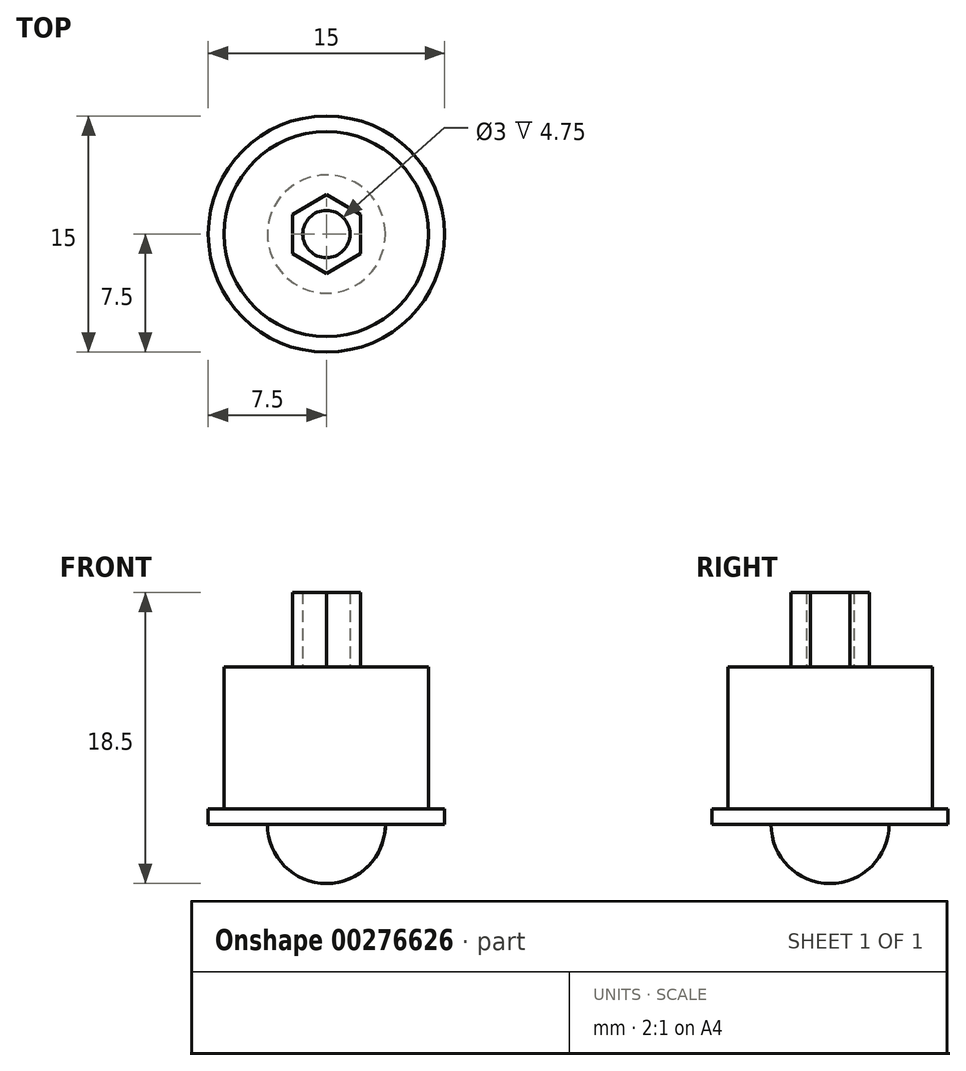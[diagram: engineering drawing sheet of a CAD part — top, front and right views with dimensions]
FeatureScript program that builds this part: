
annotation { "Feature Type Name" : "Feature", "Feature Type Description" : "" }
export const myFeature = defineFeature(function(context is Context, id is Id, definition is map)
    precondition{}
    {
        {
            var Q0;
            Q0=qCreatedBy(makeId("Front.planeOp"),FACE);
            var sketch = newSketch(context, id + "F0", { "sketchPlane" : qUnion([Q0])});
            skArc(sketch, "E0", {"start": v(0, -3.75) * mm, "mid": v(3.75, 0) * mm, "end": v(0, 3.75) * mm});
            skLineSegment(sketch, "E1", {"start": v(0, 0) * mm, "end": v(7.5, 0) * mm});
            skLineSegment(sketch, "E2", {"start": v(7.5, 0) * mm, "end": v(7.5, 1) * mm});
            skLineSegment(sketch, "E3", {"start": v(7.5, 1) * mm, "end": v(6.5, 1) * mm});
            skLineSegment(sketch, "E4", {"start": v(6.5, 1) * mm, "end": v(6.5, 10) * mm});
            skLineSegment(sketch, "E5", {"start": v(6.5, 10) * mm, "end": v(0, 10) * mm});
            skLineSegment(sketch, "E6", {"start": v(0, 10) * mm, "end": v(0, -3.75) * mm});
            skSolve(sketch);
        }
        {
            var Q0;
            Q0 = qSketchRegion(id + "F0", true);
            var Q1;
            Q1=sQuery(id+"F0.wireOp",EDGE,"E6");
            revolve(context, id + "F1", {"entities" : qUnion([Q0]), "axis" : qUnion([Q1]), "revolveType" : RevolveType.FULL});
        }
        {
            var Q0;
            Q0=makeQuery(id+"F1.opRevolve","SWEPT_FACE",FACE,{"disambiguationData":[OSD([sQuery(id+"F0.wireOp",EDGE,"E5")])]});
            var sketch = newSketch(context, id + "F2", { "sketchPlane" : qUnion([Q0])});
            skCircle(sketch, "E7", {"center": v(0, 0) * mm, "radius": 2.5 * mm, "construction": true});
            skLineSegment(sketch, "E8", {"start": v(0, 0) * mm, "end": v(0, 2.5) * mm, "construction": true});
            skCircle(sketch, "E9", {"center": v(0, 2.5) * mm, "radius": 2.5 * mm, "construction": true});
            skCircle(sketch, "E10", {"center": v(0, -2.5) * mm, "radius": 2.5 * mm, "construction": true});
            skLineSegment(sketch, "E11", {"start": v(0, 2.5) * mm, "end": v(-2.17, 1.25) * mm});
            skLineSegment(sketch, "E12", {"start": v(-2.17, 1.25) * mm, "end": v(-2.17, -1.25) * mm});
            skLineSegment(sketch, "E13", {"start": v(-2.17, -1.25) * mm, "end": v(0, -2.5) * mm});
            skLineSegment(sketch, "E14", {"start": v(0, -2.5) * mm, "end": v(2.17, -1.25) * mm});
            skLineSegment(sketch, "E15", {"start": v(2.17, -1.25) * mm, "end": v(2.17, 1.25) * mm});
            skLineSegment(sketch, "E16", {"start": v(2.17, 1.25) * mm, "end": v(0, 2.5) * mm});
            skCircle(sketch, "E17", {"center": v(0, 0) * mm, "radius": 1.5 * mm});
            skSolve(sketch);
        }
        {
            var Q0;
            Q0 = qSketchRegion(id + "F2", true);
            extrude(context, id + "F3", {"entities" : qUnion([Q0]), "operationType" : NewBodyOperationType.ADD, "depth" : 4.75 * mm});
        }
    });
